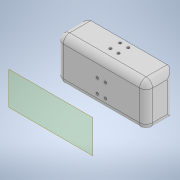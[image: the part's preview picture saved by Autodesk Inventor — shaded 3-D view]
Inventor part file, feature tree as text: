
AUTODESK INVENTOR PART (.ipt)
format: ipt  version: 2021 (Build 250183000, 183)  size: 174,080 bytes
history: native  units: mm
features: extrude x3, sketch x3, mirror x2, other x1, fillet x1, plane x1
ambient origin geometry x8: Origin, YZ Plane, XZ Plane, XY Plane, X Axis, Y Axis, Z Axis, Center Point
bodies: Body1 (feature_tree)
feature tree (11):
  other  "Sólido1"
  extrude  "Extrusión1"  Depth=10.0mm
  extrude  "Extrusión2"  Depth=8.0mm TaperAngle=0.0deg
  extrude  "Extrusión3"  Depth=9.0mm
  fillet  "Empalme1"  Radius=45.0mm
  mirror  "Simetría1"
  plane  "Plano de trabajo3"
  mirror  "Simetría3"
  sketch  "Boceto1"  dims[d0=24.0mm d4=10.0mm]
  sketch  "Boceto2"  dims[d7=5.0mm d11=8.0mm d12=0.0mm]
  sketch  "Boceto3"  dims[d15=24.5mm d16=9.0mm d17=45.0mm d18=0.0mm d24=45.0mm d25=0.0mm d26=8.0mm d28=62.25mm d19=0.5mm d20=0.872665mm]
